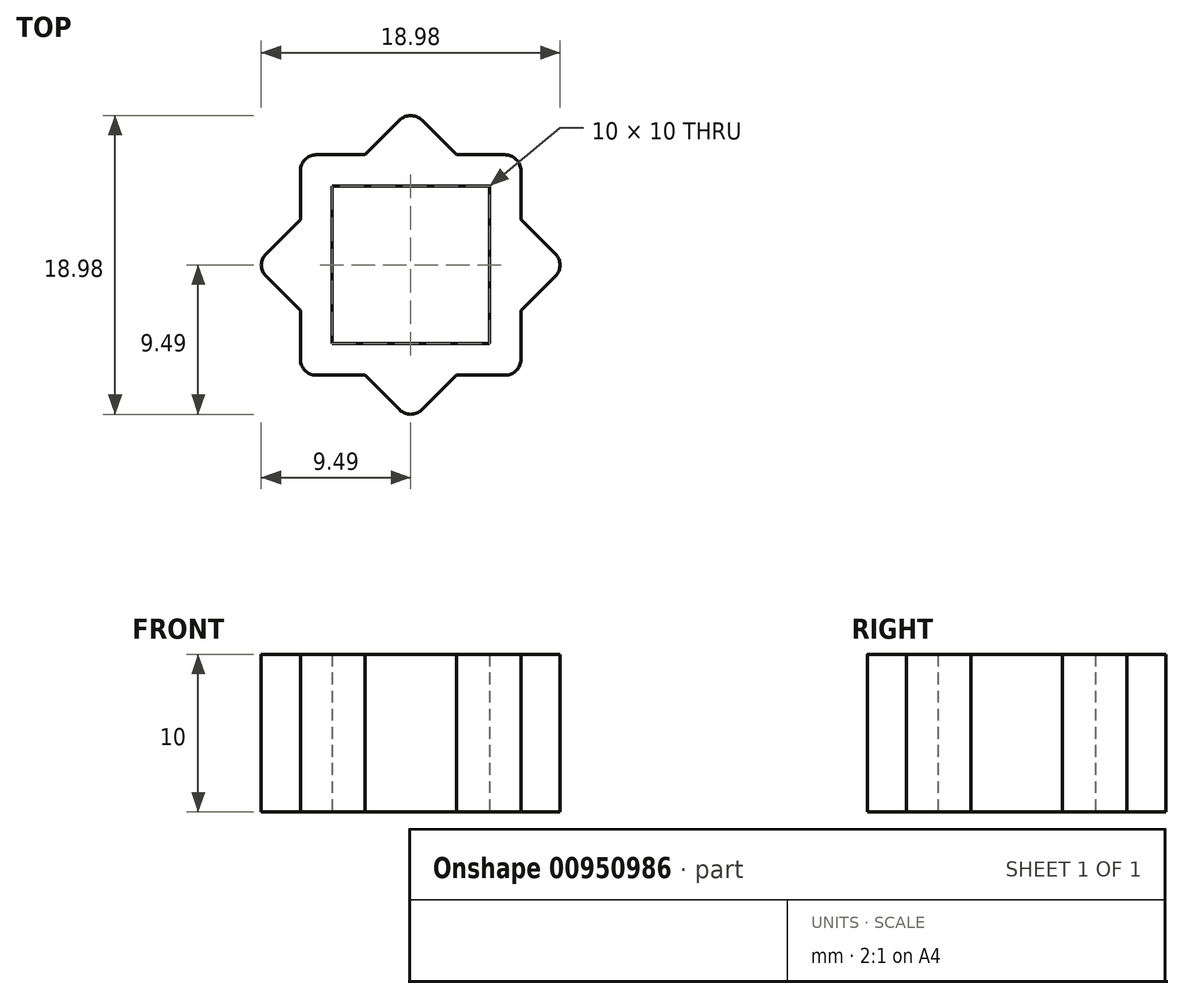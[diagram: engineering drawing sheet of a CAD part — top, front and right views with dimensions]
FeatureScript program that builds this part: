
annotation { "Feature Type Name" : "Feature", "Feature Type Description" : "" }
export const myFeature = defineFeature(function(context is Context, id is Id, definition is map)
    precondition{}
    {
        {
            var Q0;
            Q0=qCreatedBy(makeId("Top.planeOp"),FACE);
            var sketch = newSketch(context, id + "F0", { "sketchPlane" : qUnion([Q0])});
            skLineSegment(sketch, "E0.bottom", {"start": v(-6, 7) * mm, "end": v(6, 7) * mm});
            skLineSegment(sketch, "E0.top", {"start": v(-6, -7) * mm, "end": v(6, -7) * mm});
            skLineSegment(sketch, "E0.left", {"start": v(-7, 6) * mm, "end": v(-7, -6) * mm});
            skLineSegment(sketch, "E0.right", {"start": v(7, 6) * mm, "end": v(7, -6) * mm});
            skLineSegment(sketch, "E1", {"start": v(0.7, 9.2) * mm, "end": v(9.2, 0.7) * mm});
            skLineSegment(sketch, "E2", {"start": v(9.2, -0.7) * mm, "end": v(0.7, -9.2) * mm});
            skPoint(sketch, "E2.endSnap0", {"position": v(0, -7) * mm});
            skLineSegment(sketch, "E3", {"start": v(-0.7, -9.2) * mm, "end": v(-9.2, -0.7) * mm});
            skLineSegment(sketch, "E4", {"start": v(-9.2, 0.7) * mm, "end": v(-0.7, 9.2) * mm});
            skPoint(sketch, "E5.visualSharp", {"position": v(0, 9.9) * mm});
            skArc(sketch, "E5.filletArc", {"start": v(0.7, 9.2) * mm, "mid": v(0, 9.49) * mm, "end": v(-0.7, 9.2) * mm});
            skPoint(sketch, "E6.visualSharp", {"position": v(9.9, 0) * mm});
            skArc(sketch, "E6.filletArc", {"start": v(9.2, -0.7) * mm, "mid": v(9.49, 0) * mm, "end": v(9.2, 0.7) * mm});
            skPoint(sketch, "E7.visualSharp", {"position": v(0, -9.9) * mm});
            skArc(sketch, "E7.filletArc", {"start": v(-0.7, -9.2) * mm, "mid": v(0, -9.49) * mm, "end": v(0.7, -9.2) * mm});
            skPoint(sketch, "E8.visualSharp", {"position": v(-9.9, 0) * mm});
            skArc(sketch, "E8.filletArc", {"start": v(-9.2, 0.7) * mm, "mid": v(-9.49, 0) * mm, "end": v(-9.2, -0.7) * mm});
            skPoint(sketch, "E9.visualSharp", {"position": v(-7, 7) * mm});
            skArc(sketch, "E9.filletArc", {"start": v(-6, 7) * mm, "mid": v(-6.7, 6.7) * mm, "end": v(-7, 6) * mm});
            skPoint(sketch, "E10.visualSharp", {"position": v(7, 7) * mm});
            skArc(sketch, "E10.filletArc", {"start": v(7, 6) * mm, "mid": v(6.7, 6.7) * mm, "end": v(6, 7) * mm});
            skPoint(sketch, "E11.visualSharp", {"position": v(7, -7) * mm});
            skArc(sketch, "E11.filletArc", {"start": v(6, -7) * mm, "mid": v(6.7, -6.7) * mm, "end": v(7, -6) * mm});
            skPoint(sketch, "E12.visualSharp", {"position": v(-7, -7) * mm});
            skArc(sketch, "E12.filletArc", {"start": v(-7, -6) * mm, "mid": v(-6.7, -6.7) * mm, "end": v(-6, -7) * mm});
            skLineSegment(sketch, "E13.bottom", {"start": v(-5, 5) * mm, "end": v(5, 5) * mm});
            skLineSegment(sketch, "E13.top", {"start": v(-5, -5) * mm, "end": v(5, -5) * mm});
            skLineSegment(sketch, "E13.left", {"start": v(-5, 5) * mm, "end": v(-5, -5) * mm});
            skLineSegment(sketch, "E13.right", {"start": v(5, 5) * mm, "end": v(5, -5) * mm});
            skSolve(sketch);
        }
        {
            var Q0;
            Q0 = qSketchRegion(id + "F0", true);
            extrude(context, id + "F1", {"entities" : qUnion([Q0]), "depth" : 10 * mm, "offsetDistance" : 25 * mm});
        }
    });
